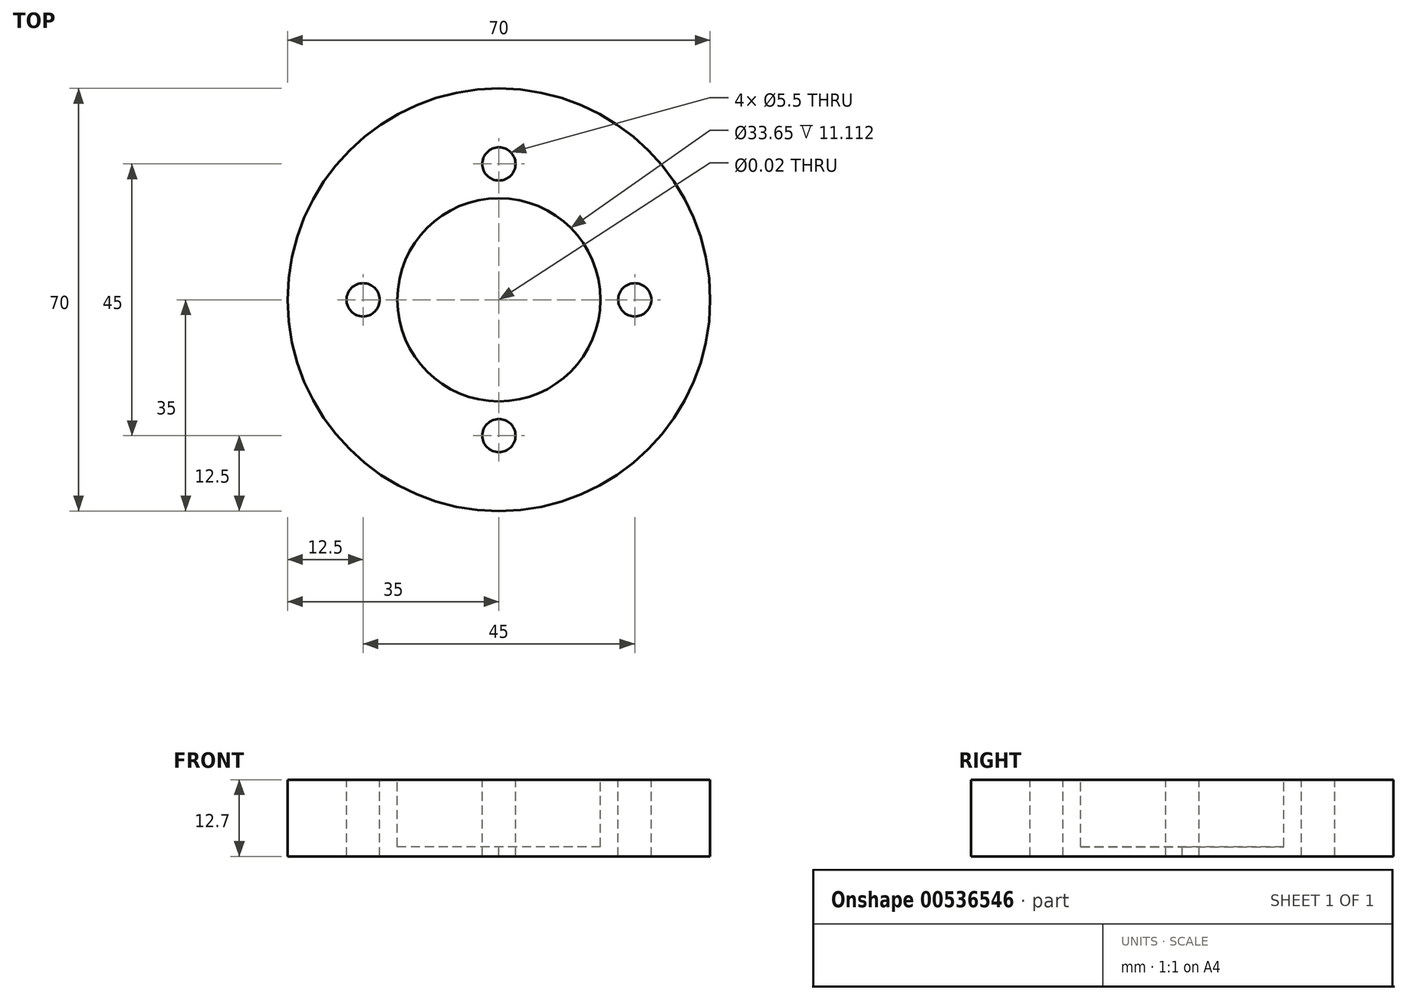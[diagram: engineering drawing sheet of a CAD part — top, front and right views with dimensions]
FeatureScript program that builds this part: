
annotation { "Feature Type Name" : "Feature", "Feature Type Description" : "" }
export const myFeature = defineFeature(function(context is Context, id is Id, definition is map)
    precondition{}
    {
        {
            var Q0;
            Q0=qCreatedBy(makeId("Front.planeOp"),FACE);
            var sketch = newSketch(context, id + "F0", { "sketchPlane" : qUnion([Q0])});
            skLineSegment(sketch, "E0.bottom", {"start": v(-38.1, 0) * mm, "end": v(53.98, 0) * mm});
            skLineSegment(sketch, "E0.top", {"start": v(-38.1, 12.7) * mm, "end": v(53.98, 12.7) * mm});
            skLineSegment(sketch, "E0.left", {"start": v(-38.1, 0) * mm, "end": v(-38.1, 12.7) * mm});
            skLineSegment(sketch, "E0.right", {"start": v(53.98, 0) * mm, "end": v(53.98, 12.7) * mm});
            skSolve(sketch);
        }
        {
            var Q0;
            Q0 = qSketchRegion(id + "F0", true);
            extrude(context, id + "F1", {"entities" : qUnion([Q0]), "endBound" : BoundingType.SYMMETRIC, "depth" : 92.07 * mm, "offsetDistance" : 25.4 * mm});
        }
        {
            var Q0;
            Q0=makeQuery(id+"F1.opExtrude","SWEPT_FACE",FACE,{"disambiguationData":[OSD([sQuery(id+"F0.wireOp",EDGE,"E0.top")])]});
            var sketch = newSketch(context, id + "F2", { "sketchPlane" : qUnion([Q0])});
            skCircle(sketch, "E1", {"center": v(0, 0) * mm, "radius": 16.83 * mm});
            skCircle(sketch, "E2", {"center": v(0, 0) * mm, "radius": 22.5 * mm, "construction": true});
            skPoint(sketch, "E3", {"position": v(0, 22.5) * mm});
            skPoint(sketch, "E4.1.0", {"position": v(-22.5, 0) * mm});
            skPoint(sketch, "E4.2.0", {"position": v(0, -22.5) * mm});
            skPoint(sketch, "E4.3.0", {"position": v(22.5, 0) * mm});
            skSolve(sketch);
        }
        {
            var Q0;
            Q0 = qSketchRegion(id + "F2", true);
            extrude(context, id + "F3", {"entities" : qUnion([Q0]), "operationType" : NewBodyOperationType.REMOVE, "oppositeDirection" : true, "depth" : 11.1 * mm, "offsetDistance" : 25.4 * mm});
        }
        {
            var Q0;
            Q0=sQuery(id+"F2.wireOp",VERTEX,"E3");
            var Q1;
            Q1=sQuery(id+"F2.wireOp",VERTEX,"E4.3.0");
            var Q2;
            Q2=sQuery(id+"F2.wireOp",VERTEX,"E4.2.0");
            var Q3;
            Q3=sQuery(id+"F2.wireOp",VERTEX,"E4.1.0");
            var Q4;
            Q4=makeQuery(id+"F1.opExtrude","SWEPT_BODY",BODY,{"disambiguationData":[OSD([sQuery(id+"F0.wireOp",EDGE,"E0.bottom"),sQuery(id+"F0.wireOp",EDGE,"E0.top"),sQuery(id+"F0.wireOp",EDGE,"E0.left"),sQuery(id+"F0.wireOp",EDGE,"E0.right")])]});
            hole(context, id + "F4", {"style" : HoleStyle.SIMPLE, "endStyle" : HoleEndStyle.THROUGH, "standardTappedOrClearance" : lookupTablePath({ "standard" : "ISO", "fit" : "Normal", "size" : "M5", "type" : "Clearance" }), "standardBlindInLast" : lookupTablePath({ "fit" : "Standard", "standard" : "ISO", "size" : "M5", "type" : "Clearance" }), "holeDiameter" : 5.5 * mm, "isTappedThrough" : true, "tappedDepth" : 15.88 * mm, "tapClearance" : 3, "startFromSketch" : true, "locations" : qUnion([Q0, Q1, Q2, Q3]), "scope" : qUnion([Q4])});
        }
        {
            var Q0;
            Q0=makeQuery(id+"F2.imprint","IMPRINT",FACE,{"disambiguationData":[TD([[makeQuery(id+"F2.imprint","IMPRINT",EDGE,{"derivedFrom":sQuery(id+"F2.wireOp",EDGE,"E1")}),-1.0]])]});
            var sketch = newSketch(context, id + "F5", { "sketchPlane" : qUnion([Q0])});
            skCircle(sketch, "E5", {"center": v(0, 0) * mm, "radius": 35 * mm});
            skSolve(sketch);
        }
        {
            var Q0;
            Q0=makeQuery(id+"F5.imprint","IMPRINT",FACE,{"disambiguationData":[TD([[makeQuery(id+"F5.imprint","IMPRINT",EDGE,{"derivedFrom":makeQuery(id+"F2.imprint","IMPRINT",EDGE,{"derivedFrom":sQuery(id+"F2.wireOp",EDGE,"E1")})}),1.0]])]});
            var Q1;
            Q1=makeQuery(id+"F5.imprint","IMPRINT",FACE,{"disambiguationData":[TD([[makeQuery(id+"F5.imprint","IMPRINT",EDGE,{"derivedFrom":sQuery(id+"F5.wireOp",EDGE,"E5")}),1.0]])]});
            extrude(context, id + "F6", {"entities" : qUnion([Q0, Q1]), "operationType" : NewBodyOperationType.INTERSECT, "oppositeDirection" : true, "depth" : 25.4 * mm, "offsetDistance" : 25.4 * mm});
        }
        {
            var Q0;
            Q0=sQuery(id+"F2.wireOp",VERTEX,"E1.center");
            var Q1;
            Q1=makeQuery(id+"F1.opExtrude","SWEPT_BODY",BODY,{"disambiguationData":[OSD([sQuery(id+"F0.wireOp",EDGE,"E0.bottom"),sQuery(id+"F0.wireOp",EDGE,"E0.top"),sQuery(id+"F0.wireOp",EDGE,"E0.left"),sQuery(id+"F0.wireOp",EDGE,"E0.right")])]});
            hole(context, id + "F7", {"style" : HoleStyle.C_BORE, "endStyle" : HoleEndStyle.THROUGH, "standardTappedOrClearance" : lookupTablePath({ "standard" : "ANSI", "size" : "1/2 (0.5)", "type" : "Drilled" }), "standardBlindInLast" : lookupTablePath({ "standard" : "ANSI", "size" : "1/2", "type" : "Drilled" }), "holeDiameter" : 1 / 50.8 * mm, "cBoreDiameter" : 1 / 50.8 * mm, "cBoreDepth" : 6.35 * mm, "isTappedThrough" : true, "tappedDepth" : 15.88 * mm, "tapClearance" : 3, "startFromSketch" : true, "locations" : qUnion([Q0]), "scope" : qUnion([Q1])});
        }
    });
